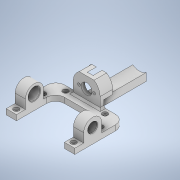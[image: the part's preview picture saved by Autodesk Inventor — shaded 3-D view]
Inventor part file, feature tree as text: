
AUTODESK INVENTOR PART (.ipt)
format: ipt  version: 2022.6 (Build 266554000, 554)  size: 340,992 bytes
history: native  units: mm
features: sketch x12, projected_geometry x10, extrude x8, hole x4, chamfer x2, thicken_offset x1, fillet x1, mirror x1
ambient origin geometry x8: Origin, YZ Plane, XZ Plane, XY Plane, X Axis, Y Axis, Z Axis, Center Point
bodies: Solid1 (feature_tree)
feature tree (39):
  extrude  "Extrusion1"  Depth=55.5mm
  extrude  "Extrusion2"  Depth=12.0mm
  extrude  "Extrusion5"  Depth=12.5mm TaperAngle=0.0deg
  hole  "Shaft Hole"  [1 undecoded]
  hole  "Hole4"  [1 undecoded]
  hole  "Hole5"  [1 undecoded]
  extrude  "Extrusion6"  Depth=8.0mm
  thicken_offset  "Thicken1"
  extrude  "Extrusion7"  Depth=10.0mm
  fillet  "Fillet1"  Radius=10.0mm
  extrude  "Extrusion8"  Depth=15.0mm
  hole  "Hole6"  [1 undecoded]
  extrude  "Extrusion9"  Depth=10.0mm
  mirror  "Mirror1"
  chamfer  "Chamfer1"  Distance=10.0mm
  extrude  "Extrusion10"  Depth=10.0mm
  chamfer  "Chamfer2"  Distance=20.0mm
  sketch  "Sketch1"  dims[d0=76.5mm d1=55.5mm]
  sketch  "Sketch2"  dims[d2=6.0mm d3=0.0mm d4=12.0mm]
  projected_geometry  "Projected Loop1"
  sketch  "Sketch6"  dims[d5=11.5mm d9=12.5mm d10=0.0mm]
  projected_geometry  "Projected Loop5"
  sketch  "Sketch7"  dims[d37=4.0mm d38=30.0mm]
  projected_geometry  "Projected Loop6"
  sketch  "Sketch8"  dims[d39=55.0mm d40=0.0mm]
  sketch  "Sketch9"  dims[d41=12.0mm d42=6.0mm d43=4.0mm d44=2.0mm d45=90.0deg d46=8.0mm d47=20.594885mm d48=5.0mm]
  projected_geometry  "Projected Loop7"
  sketch  "Sketch10"  dims[d49=3.4mm d50=6.0mm d51=6.0mm d52=2.0mm d53=90.0deg d54=8.0mm d55=20.594885mm d56=6.25mm]
  projected_geometry  "Projected Loop8"
  sketch  "Sketch11"  dims[d58=17.0mm]
  projected_geometry  "Projected Loop9"
  sketch  "Sketch13"  dims[d59=3.0mm d60=6.0mm d61=6.0mm d62=2.0mm d63=90.0deg d64=8.0mm d65=20.594885mm d66=5.0mm]
  projected_geometry  "Projected Loop10"
  sketch  "Sketch14"  dims[d67=25.0mm d68=5.0mm d69=10.0mm d70=0.0mm]
  projected_geometry  "Projected Loop11"
  sketch  "Sketch15"  dims[d71=0.4mm d72=1.0mm d73=15.0mm]
  projected_geometry  "Projected Loop12"
  sketch  "Sketch16"  dims[d74=25.0mm d75=55.0mm d76=0.0mm d77=10.0mm d78=10.0mm d79=10.0mm d80=20.0mm d81=55.0mm d82=0.0mm d83=13.3mm d84=6.0mm d85=4.0mm d86=2.0mm d87=90.0deg d88=8.0mm d89=20.594885mm d90=1.0mm d91=1.0mm d92=0.0mm d93=0.5mm d94=2.0mm d95=45.0deg d96=30.0mm d98=15.0mm d99=10.0mm d101=3.0mm d102=12.5mm d103=0.0mm d104=0.0mm d105=2.0mm d106=2.0mm d107=45.0deg]
  projected_geometry  "Projected Loop13"
note: 4 required parameter values undecoded (feature->parameter linkage not recoverable at this tier; creation-order binding heuristic only, values carry confidence <= 0.55)
